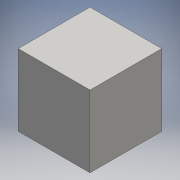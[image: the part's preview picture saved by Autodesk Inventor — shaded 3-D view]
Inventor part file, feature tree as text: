
AUTODESK INVENTOR PART (.ipt)
format: ipt  version: 2016 (Build 200138000, 138)  size: 80,384 bytes
history: native  units: mm
features: extrude x1, sketch x1
ambient origin geometry x8: Origin, YZ Plane, XZ Plane, XY Plane, X Axis, Y Axis, Z Axis, Center Point
bodies: Solid1 (feature_tree)
feature tree (2):
  extrude  "Extrusion1"  Depth=60.0mm
  sketch  "Sketch1"  dims[d0=60.0mm d1=60.0mm d2=60.0mm d3=0.0mm]
